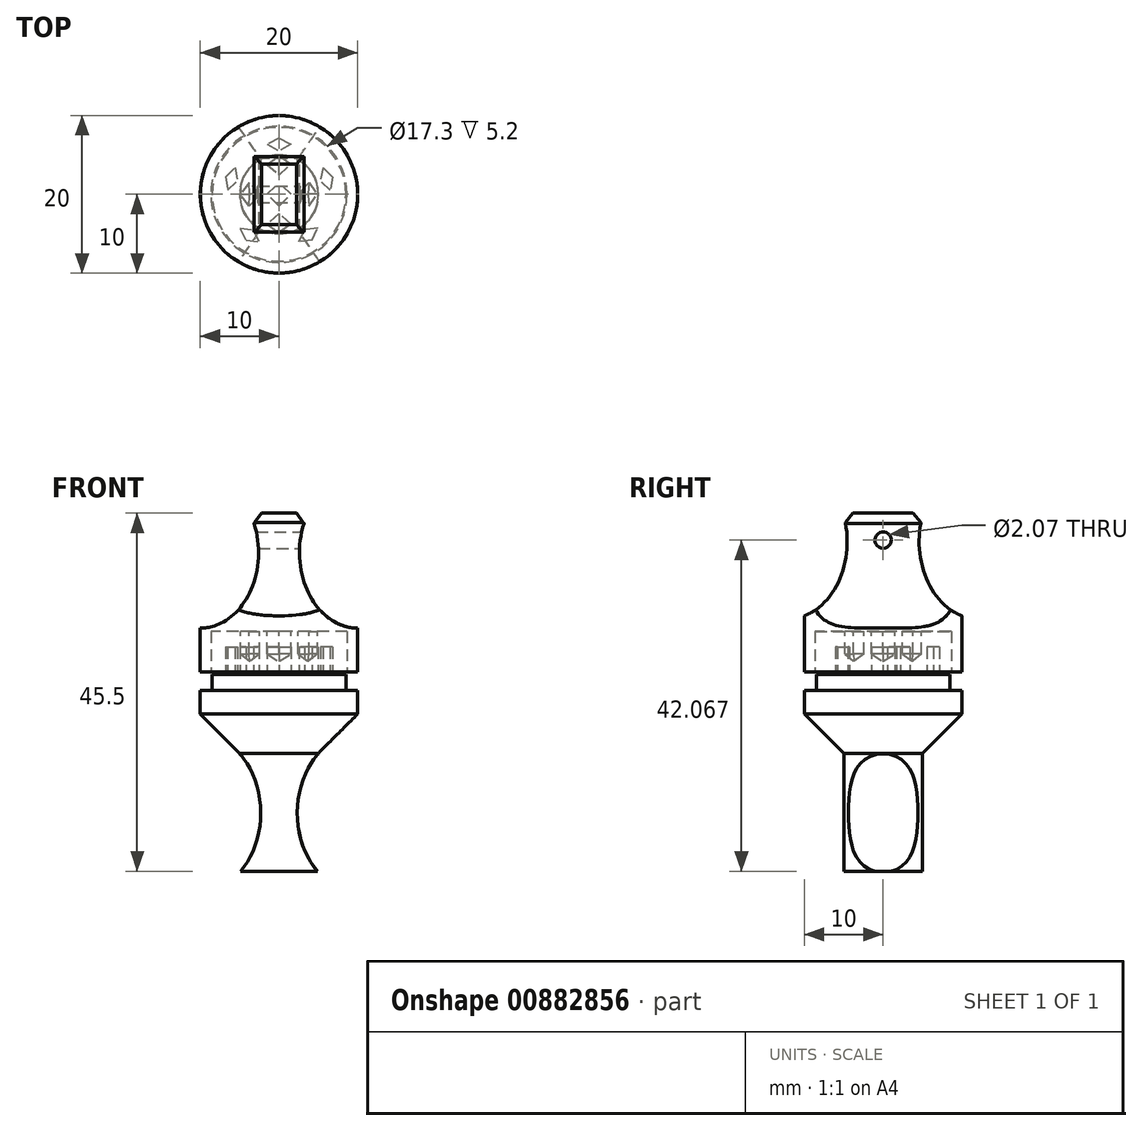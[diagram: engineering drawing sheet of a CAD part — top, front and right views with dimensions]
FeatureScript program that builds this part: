
annotation { "Feature Type Name" : "Feature", "Feature Type Description" : "" }
export const myFeature = defineFeature(function(context is Context, id is Id, definition is map)
    precondition{}
    {
        {
            var Q0;
            Q0=qCreatedBy(makeId("Top.planeOp"),FACE);
            var sketch = newSketch(context, id + "F0", { "sketchPlane" : qUnion([Q0])});
            skCircle(sketch, "E0", {"center": v(0, 0) * mm, "radius": 10 * mm});
            skSolve(sketch);
        }
        {
            var Q0;
            Q0=makeQuery(id+"F0.imprint","IMPRINT",FACE,{"disambiguationData":[TD([[makeQuery(id+"F0.imprint","IMPRINT",EDGE,{"derivedFrom":sQuery(id+"F0.wireOp",EDGE,"E0")}),1.0]])]});
            extrude(context, id + "F1", {"entities" : qUnion([Q0]), "depth" : 3 * mm, "offsetDistance" : 25 * mm});
        }
        {
            var Q0;
            Q0=makeQuery(id+"F1.opExtrude","CAP_FACE",FACE,{"disambiguationData":[OSD([sQuery(id+"F0.wireOp",EDGE,"E0")])],"isStart":false});
            var sketch = newSketch(context, id + "F2", { "sketchPlane" : qUnion([Q0])});
            skCircle(sketch, "E1", {"center": v(0, 0) * mm, "radius": 8.5 * mm});
            skSolve(sketch);
        }
        {
            var Q0;
            Q0 = qSketchRegion(id + "F2", true);
            extrude(context, id + "F3", {"entities" : qUnion([Q0]), "operationType" : NewBodyOperationType.ADD, "depth" : 2 * mm, "offsetDistance" : 25 * mm});
        }
        {
            var Q0;
            Q0=makeQuery(id+"F3.opExtrude","CAP_FACE",FACE,{"disambiguationData":[OSD([sQuery(id+"F2.wireOp",EDGE,"E1")])],"isStart":false});
            var sketch = newSketch(context, id + "F4", { "sketchPlane" : qUnion([Q0])});
            skLineSegment(sketch, "E2", {"start": v(0, 0) * mm, "end": v(0, 6.36) * mm});
            skLineSegment(sketch, "E3", {"start": v(0, 6.36) * mm, "end": v(0, 7.16) * mm});
            skLineSegment(sketch, "E4", {"start": v(0, 7.16) * mm, "end": v(1.5, 6.36) * mm});
            skLineSegment(sketch, "E5", {"start": v(1.5, 6.36) * mm, "end": v(0, 5.54) * mm});
            skLineSegment(sketch, "E6.MirrorCS", {"start": v(-1.5, 6.36) * mm, "end": v(0, 5.54) * mm});
            skLineSegment(sketch, "E7.MirrorCS", {"start": v(0, 7.16) * mm, "end": v(-1.5, 6.36) * mm});
            skLineSegment(sketch, "E8.1.0", {"start": v(-6.81, 2.21) * mm, "end": v(-5.59, 3.4) * mm});
            skLineSegment(sketch, "E8.1.1", {"start": v(-6.52, 0.54) * mm, "end": v(-5.27, 1.71) * mm});
            skLineSegment(sketch, "E8.1.2", {"start": v(-5.59, 3.4) * mm, "end": v(-5.27, 1.71) * mm});
            skLineSegment(sketch, "E8.1.3", {"start": v(-6.81, 2.21) * mm, "end": v(-6.52, 0.54) * mm});
            skLineSegment(sketch, "E8.2.0", {"start": v(-4.21, -5.8) * mm, "end": v(-4.96, -4.26) * mm});
            skLineSegment(sketch, "E8.2.1", {"start": v(-2.52, -6.03) * mm, "end": v(-3.25, -4.48) * mm});
            skLineSegment(sketch, "E8.2.2", {"start": v(-4.96, -4.26) * mm, "end": v(-3.25, -4.48) * mm});
            skLineSegment(sketch, "E8.2.3", {"start": v(-4.21, -5.8) * mm, "end": v(-2.52, -6.03) * mm});
            skPoint(sketch, "E8.center", {"position": v(0, 0) * mm});
            skLineSegment(sketch, "E9.1.3.0", {"start": v(4.21, -5.8) * mm, "end": v(2.52, -6.03) * mm});
            skLineSegment(sketch, "E9.3.3.0", {"start": v(4.96, -4.26) * mm, "end": v(3.25, -4.48) * mm});
            skLineSegment(sketch, "E9.6.3.0", {"start": v(2.52, -6.03) * mm, "end": v(3.25, -4.48) * mm});
            skLineSegment(sketch, "E9.9.3.0", {"start": v(4.21, -5.8) * mm, "end": v(4.96, -4.26) * mm});
            skLineSegment(sketch, "E9.1.4.0", {"start": v(6.81, 2.21) * mm, "end": v(6.52, 0.54) * mm});
            skLineSegment(sketch, "E9.3.4.0", {"start": v(5.59, 3.4) * mm, "end": v(5.27, 1.71) * mm});
            skLineSegment(sketch, "E9.6.4.0", {"start": v(6.52, 0.54) * mm, "end": v(5.27, 1.71) * mm});
            skLineSegment(sketch, "E9.9.4.0", {"start": v(6.81, 2.21) * mm, "end": v(5.59, 3.4) * mm});
            skSolve(sketch);
        }
        {
            var Q0;
            Q0=makeQuery(id+"F4.imprint","IMPRINT",FACE,{"disambiguationData":[TD([[makeQuery(id+"F4.imprint","IMPRINT",EDGE,{"derivedFrom":sQuery(id+"F4.wireOp",EDGE,"E4")}),1.0]])]});
            var sketch = newSketch(context, id + "F5", { "sketchPlane" : qUnion([Q0])});
            skLineSegment(sketch, "E10", {"start": v(1.5, 0) * mm, "end": v(0, 0) * mm});
            skLineSegment(sketch, "E11", {"start": v(-1.5, 0) * mm, "end": v(0, 1.5) * mm});
            skLineSegment(sketch, "E12", {"start": v(1.5, 0) * mm, "end": v(0, 1.5) * mm});
            skLineSegment(sketch, "E13", {"start": v(0, -1.5) * mm, "end": v(1.5, 0) * mm});
            skLineSegment(sketch, "E14", {"start": v(0, -1.5) * mm, "end": v(-1.5, 0) * mm});
            skSolve(sketch);
        }
        {
            var Q0;
            Q0 = qSketchRegion(id + "F5", true);
            var Q1;
            Q1 = qSketchRegion(id + "F4", true);
            extrude(context, id + "F6", {"entities" : qUnion([Q0, Q1]), "operationType" : NewBodyOperationType.ADD, "depth" : 3.5 * mm, "offsetDistance" : 25 * mm});
        }
        {
            var Q0;
            Q0=makeQuery(id+"F1.opExtrude","CAP_FACE",FACE,{"disambiguationData":[OSD([sQuery(id+"F0.wireOp",EDGE,"E0")])],"isStart":true});
            extrude(context, id + "F7", {"entities" : qUnion([Q0]), "operationType" : NewBodyOperationType.ADD, "depth" : 5 * mm, "offsetDistance" : 25 * mm});
        }
        {
            var Q0;
            Q0=makeQuery(id+"F7.opExtrude","CAP_EDGE",EDGE,{"disambiguationData":[OSD([sQuery(id+"F0.wireOp",EDGE,"E0")])],"isStart":false});
            chamfer(context, id + "F8", {"entities" : qUnion([Q0]), "width" : 5 * mm, "tangentPropagation" : true});
        }
        {
            var Q0;
            Q0=makeQuery(id+"F7.opExtrude","CAP_FACE",FACE,{"disambiguationData":[OSD([sQuery(id+"F0.wireOp",EDGE,"E0")])],"isStart":false});
            extrude(context, id + "F9", {"entities" : qUnion([Q0]), "operationType" : NewBodyOperationType.ADD, "depth" : 15 * mm, "offsetDistance" : 25 * mm});
        }
        {
            var Q0;
            Q0=qCreatedBy(makeId("Front.planeOp"),FACE);
            var sketch = newSketch(context, id + "F10", { "sketchPlane" : qUnion([Q0])});
            skLineSegment(sketch, "E15", {"start": v(0, -12.6) * mm, "end": v(9.76, -12.6) * mm});
            skEllipse(sketch, "E16", {"center": v(9.76, -12.6) * mm, "majorRadius": 7.43 * mm, "minorRadius": 9.76 * mm, "majorAxis": v(-1, 0)});
            skEllipse(sketch, "E17.MirrorC", {"center": v(-9.76, -12.6) * mm, "majorRadius": 7.43 * mm, "minorRadius": 9.76 * mm, "majorAxis": v(1, 0)});
            skSolve(sketch);
        }
        {
            var Q0;
            Q0=makeQuery(id+"F10.imprint","IMPRINT",FACE,{"disambiguationData":[TD([[makeQuery(id+"F10.imprint","IMPRINT",EDGE,{"derivedFrom":sQuery(id+"F10.wireOp",EDGE,"E16")}),1.0]])]});
            var Q1;
            Q1=makeQuery(id+"F10.imprint","IMPRINT",FACE,{"disambiguationData":[TD([[makeQuery(id+"F10.imprint","IMPRINT",EDGE,{"derivedFrom":sQuery(id+"F10.wireOp",EDGE,"E17.MirrorC")}),1.0]])]});
            extrude(context, id + "F11", {"entities" : qUnion([Q0, Q1]), "operationType" : NewBodyOperationType.REMOVE, "endBound" : BoundingType.SYMMETRIC, "oppositeDirection" : true, "depth" : 25 * mm, "offsetDistance" : 25 * mm});
        }
        {
            var Q0;
            Q0=makeQuery(id+"F6.opExtrude","CAP_FACE",FACE,{"disambiguationData":[OSD([sQuery(id+"F5.wireOp",EDGE,"E11"),sQuery(id+"F5.wireOp",EDGE,"E12"),sQuery(id+"F5.wireOp",EDGE,"E13"),sQuery(id+"F5.wireOp",EDGE,"E14")])],"isStart":false});
            var sketch = newSketch(context, id + "F12", { "sketchPlane" : qUnion([Q0])});
            skCircle(sketch, "E18", {"center": v(0, 0) * mm, "radius": 8.65 * mm});
            skCircle(sketch, "E19", {"center": v(0, 0) * mm, "radius": 10 * mm});
            skSolve(sketch);
        }
        {
            var Q0;
            Q0=makeQuery(id+"F12.imprint","IMPRINT",FACE,{"disambiguationData":[TD([[makeQuery(id+"F12.imprint","IMPRINT",EDGE,{"derivedFrom":sQuery(id+"F12.wireOp",EDGE,"E18")}),-1.0]])]});
            extrude(context, id + "F13", {"entities" : qUnion([Q0]), "depth" : 2 * mm, "offsetDistance" : 25 * mm});
        }
        {
            var Q0;
            Q0=makeQuery(id+"F13.opExtrude","CAP_FACE",FACE,{"disambiguationData":[OSD([sQuery(id+"F12.wireOp",EDGE,"E18"),sQuery(id+"F12.wireOp",EDGE,"E19")])],"isStart":false});
            var sketch = newSketch(context, id + "F14", { "sketchPlane" : qUnion([Q0])});
            skCircle(sketch, "E20", {"center": v(0, 0) * mm, "radius": 10 * mm});
            skSolve(sketch);
        }
        {
            var Q0;
            Q0 = qSketchRegion(id + "F14", true);
            extrude(context, id + "F15", {"entities" : qUnion([Q0]), "operationType" : NewBodyOperationType.ADD, "depth" : 15 * mm, "offsetDistance" : 25 * mm});
        }
        {
            var Q0;
            Q0=qCreatedBy(makeId("Front.planeOp"),FACE);
            var sketch = newSketch(context, id + "F16", { "sketchPlane" : qUnion([Q0])});
            skLineSegment(sketch, "E21", {"start": v(0, 0) * mm, "end": v(0, 25.5) * mm});
            skLineSegment(sketch, "E22", {"start": v(0, 25.5) * mm, "end": v(0, 10.5) * mm});
            skLineSegment(sketch, "E23", {"start": v(0, 18) * mm, "end": v(9.97, 18) * mm});
            skLineSegment(sketch, "E24", {"start": v(9.97, 18) * mm, "end": v(9.97, 20.5) * mm});
            skEllipse(sketch, "E25", {"center": v(9.97, 20.5) * mm, "majorRadius": 7.37 * mm, "minorRadius": 9.6 * mm, "majorAxis": v(-1, 0)});
            skEllipse(sketch, "E26.MirrorC", {"center": v(-9.97, 20.5) * mm, "majorRadius": 7.37 * mm, "minorRadius": 9.6 * mm, "majorAxis": v(1, 0)});
            skSolve(sketch);
        }
        {
            var Q0;
            Q0=makeQuery(id+"F16.imprint","IMPRINT",FACE,{"disambiguationData":[TD([[makeQuery(id+"F16.imprint","IMPRINT",EDGE,{"derivedFrom":sQuery(id+"F16.wireOp",EDGE,"E26.MirrorC")}),1.0]])]});
            var Q1;
            Q1=makeQuery(id+"F16.imprint","IMPRINT",FACE,{"disambiguationData":[TD([[makeQuery(id+"F16.imprint","IMPRINT",EDGE,{"derivedFrom":sQuery(id+"F16.wireOp",EDGE,"E25")}),1.0]])]});
            extrude(context, id + "F17", {"entities" : qUnion([Q0, Q1]), "operationType" : NewBodyOperationType.REMOVE, "endBound" : BoundingType.SYMMETRIC, "oppositeDirection" : true, "depth" : 25 * mm, "offsetDistance" : 25 * mm});
        }
        {
            var Q0;
            Q0=qCreatedBy(makeId("Right.planeOp"),FACE);
            var sketch = newSketch(context, id + "F18", { "sketchPlane" : qUnion([Q0])});
            skEllipse(sketch, "E27", {"center": v(12.2, 21.9) * mm, "majorRadius": 9.86 * mm, "minorRadius": 7.62 * mm, "majorAxis": v(0, -1)});
            skEllipse(sketch, "E28.MirrorC", {"center": v(-12.2, 21.9) * mm, "majorRadius": 9.86 * mm, "minorRadius": 7.62 * mm, "majorAxis": v(0, -1)});
            skSolve(sketch);
        }
        {
            var Q0;
            Q0=makeQuery(id+"F18.imprint","IMPRINT",FACE,{"disambiguationData":[TD([[makeQuery(id+"F18.imprint","IMPRINT",EDGE,{"derivedFrom":sQuery(id+"F18.wireOp",EDGE,"E28.MirrorC")}),1.0]])]});
            var Q1;
            Q1=makeQuery(id+"F18.imprint","IMPRINT",FACE,{"disambiguationData":[TD([[makeQuery(id+"F18.imprint","IMPRINT",EDGE,{"derivedFrom":sQuery(id+"F18.wireOp",EDGE,"E27")}),1.0]])]});
            extrude(context, id + "F19", {"entities" : qUnion([Q0, Q1]), "operationType" : NewBodyOperationType.REMOVE, "endBound" : BoundingType.SYMMETRIC, "depth" : 25 * mm, "offsetDistance" : 25 * mm});
        }
        {
            var Q0;
            Q0=makeQuery(id+"F15.opExtrude","CAP_FACE",FACE,{"disambiguationData":[OSD([sQuery(id+"F14.wireOp",EDGE,"E20")])],"isStart":true});
            var sketch = newSketch(context, id + "F20", { "sketchPlane" : qUnion([Q0])});
            skLineSegment(sketch, "E29", {"start": v(0, 0) * mm, "end": v(0, -3.8) * mm});
            skLineSegment(sketch, "E30", {"start": v(0, -3.8) * mm, "end": v(-1.5, -3.8) * mm});
            skLineSegment(sketch, "E31.MirrorCS", {"start": v(-1.5, -3.8) * mm, "end": v(0, -4.87) * mm});
            skLineSegment(sketch, "E32.MirrorCS", {"start": v(1.5, -3.8) * mm, "end": v(0, -4.87) * mm});
            skLineSegment(sketch, "E33", {"start": v(-1.5, -3.8) * mm, "end": v(0, -2.44) * mm});
            skLineSegment(sketch, "E34", {"start": v(0, -2.44) * mm, "end": v(1.5, -3.8) * mm});
            skLineSegment(sketch, "E35.1.0", {"start": v(2.44, 0) * mm, "end": v(3.8, 1.5) * mm});
            skLineSegment(sketch, "E35.1.1", {"start": v(3.8, -1.5) * mm, "end": v(2.44, 0) * mm});
            skLineSegment(sketch, "E35.1.2", {"start": v(3.8, -1.5) * mm, "end": v(4.87, 0) * mm});
            skLineSegment(sketch, "E35.1.3", {"start": v(3.8, 1.5) * mm, "end": v(4.87, 0) * mm});
            skLineSegment(sketch, "E35.2.0", {"start": v(0, 2.44) * mm, "end": v(-1.5, 3.8) * mm});
            skLineSegment(sketch, "E35.2.1", {"start": v(1.5, 3.8) * mm, "end": v(0, 2.44) * mm});
            skLineSegment(sketch, "E35.2.2", {"start": v(1.5, 3.8) * mm, "end": v(0, 4.87) * mm});
            skLineSegment(sketch, "E35.2.3", {"start": v(-1.5, 3.8) * mm, "end": v(0, 4.87) * mm});
            skPoint(sketch, "E35.center", {"position": v(0, 0) * mm});
            skLineSegment(sketch, "E36.1.3.0", {"start": v(-2.44, 0) * mm, "end": v(-3.8, -1.5) * mm});
            skLineSegment(sketch, "E36.3.3.0", {"start": v(-3.8, 1.5) * mm, "end": v(-2.44, 0) * mm});
            skLineSegment(sketch, "E36.6.3.0", {"start": v(-3.8, 1.5) * mm, "end": v(-4.87, 0) * mm});
            skLineSegment(sketch, "E36.9.3.0", {"start": v(-3.8, -1.5) * mm, "end": v(-4.87, 0) * mm});
            skSolve(sketch);
        }
        {
            var Q0;
            Q0 = qSketchRegion(id + "F20", true);
            extrude(context, id + "F21", {"entities" : qUnion([Q0]), "operationType" : NewBodyOperationType.ADD, "depth" : 3.8 * mm, "offsetDistance" : 25 * mm});
        }
        {
            var Q0;
            Q0=makeQuery(id+"F21.opExtrude","CAP_EDGE",EDGE,{"disambiguationData":[OSD([sQuery(id+"F20.wireOp",EDGE,"E36.6.3.0")])],"isStart":false});
            var Q1;
            Q1=makeQuery(id+"F21.opExtrude","CAP_FACE",FACE,{"disambiguationData":[OSD([sQuery(id+"F20.wireOp",EDGE,"E35.2.0"),sQuery(id+"F20.wireOp",EDGE,"E35.2.1"),sQuery(id+"F20.wireOp",EDGE,"E35.2.2"),sQuery(id+"F20.wireOp",EDGE,"E35.2.3")])],"isStart":false});
            var Q2;
            Q2=makeQuery(id+"F21.opExtrude","CAP_FACE",FACE,{"disambiguationData":[OSD([sQuery(id+"F20.wireOp",EDGE,"E36.1.3.0"),sQuery(id+"F20.wireOp",EDGE,"E36.3.3.0"),sQuery(id+"F20.wireOp",EDGE,"E36.6.3.0"),sQuery(id+"F20.wireOp",EDGE,"E36.9.3.0")])],"isStart":false});
            var Q3;
            Q3=makeQuery(id+"F21.opExtrude","CAP_FACE",FACE,{"disambiguationData":[OSD([sQuery(id+"F20.wireOp",EDGE,"E31.MirrorCS"),sQuery(id+"F20.wireOp",EDGE,"E32.MirrorCS"),sQuery(id+"F20.wireOp",EDGE,"E33"),sQuery(id+"F20.wireOp",EDGE,"E34")])],"isStart":false});
            var Q4;
            Q4=makeQuery(id+"F21.opExtrude","CAP_FACE",FACE,{"disambiguationData":[OSD([sQuery(id+"F20.wireOp",EDGE,"E35.1.0"),sQuery(id+"F20.wireOp",EDGE,"E35.1.1"),sQuery(id+"F20.wireOp",EDGE,"E35.1.2"),sQuery(id+"F20.wireOp",EDGE,"E35.1.3")])],"isStart":false});
            chamfer(context, id + "F22", {"entities" : qUnion([Q0, Q1, Q2, Q3, Q4]), "width" : .9 * mm, "tangentPropagation" : true});
        }
        {
            var Q0;
            Q0=qCreatedBy(makeId("Right.planeOp"),FACE);
            var sketch = newSketch(context, id + "F23", { "sketchPlane" : qUnion([Q0])});
            skCircle(sketch, "E37", {"center": v(0, 22.07) * mm, "radius": 1.03 * mm});
            skSolve(sketch);
        }
        {
            var Q0;
            Q0 = qSketchRegion(id + "F23", true);
            extrude(context, id + "F24", {"entities" : qUnion([Q0]), "operationType" : NewBodyOperationType.REMOVE, "endBound" : BoundingType.SYMMETRIC, "oppositeDirection" : true, "depth" : 25 * mm, "offsetDistance" : 25 * mm});
        }
        {
            var Q0;
            Q0=makeQuery(id+"F17.boolean.opBoolean","INTERSECT",EDGE,{"derivedFrom":[makeQuery(id+"F15.opExtrude","CAP_FACE",FACE,{"disambiguationData":[OSD([sQuery(id+"F14.wireOp",EDGE,"E20")])],"isStart":false}),makeQuery(id+"F17.opExtrude","SWEPT_FACE",FACE,{"disambiguationData":[OSD([sQuery(id+"F16.wireOp",EDGE,"E25")])]})]});
            var Q1;
            Q1=makeQuery(id+"F15.opExtrude","CAP_FACE",FACE,{"disambiguationData":[OSD([sQuery(id+"F14.wireOp",EDGE,"E20")])],"isStart":false});
            chamfer(context, id + "F25", {"entities" : qUnion([Q0, Q1]), "width" : 1 * mm, "tangentPropagation" : true});
        }
        {
            var Q0;
            Q0=makeQuery(id+"F13.opExtrude","CAP_FACE",FACE,{"disambiguationData":[OSD([sQuery(id+"F12.wireOp",EDGE,"E18"),sQuery(id+"F12.wireOp",EDGE,"E19")])],"isStart":true});
            extrude(context, id + "F26", {"entities" : qUnion([Q0]), "operationType" : NewBodyOperationType.ADD, "depth" : 3.2 * mm, "offsetDistance" : 25 * mm});
        }
    });
